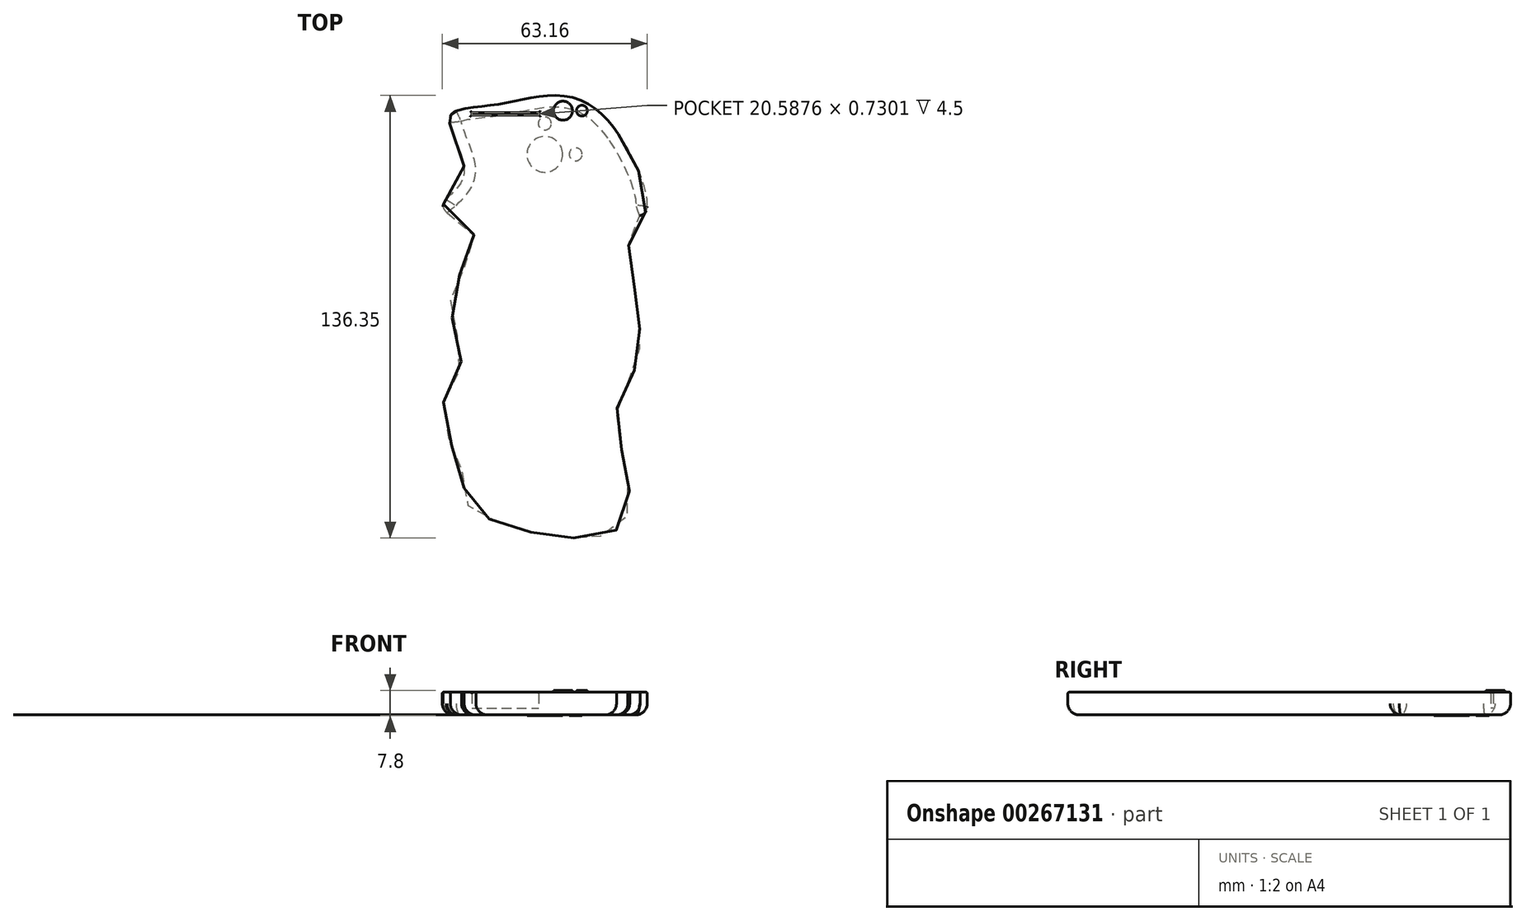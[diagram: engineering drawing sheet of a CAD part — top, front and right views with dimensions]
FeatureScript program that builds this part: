
annotation { "Feature Type Name" : "Feature", "Feature Type Description" : "" }
export const myFeature = defineFeature(function(context is Context, id is Id, definition is map)
    precondition{}
    {
        {
            var Q0;
            Q0=qCreatedBy(makeId("Top.planeOp"),FACE);
            var sketch = newSketch(context, id + "F0", { "sketchPlane" : qUnion([Q0])});
            skFitSpline(sketch, "E0", {"points": [v(-68.04, 102.87) * mm, v(-82.19, 98.83) * mm, v(-77.9, 80.9) * mm, v(-84.21, 71.3) * mm, v(-74.36, 61.95) * mm, v(-81.7, 44.48) * mm, v(-78.66, 23.47) * mm, v(-84.48, 9.04) * mm, v(-77.9, -12.47) * mm, v(-75.88, -21.33) * mm, v(-29.8, -27.4) * mm, v(-30.82, 7.58) * mm, v(-23.77, 26.7) * mm, v(-26.54, 66.97) * mm, v(-21.76, 69.99) * mm, v(-38.11, 102.2) * mm, v(-68.04, 102.87) * mm]});
            skArc(sketch, "E1", {"start": v(-30.24, 93.84) * mm, "mid": v(-56.07, 97.58) * mm, "end": v(-82.17, 97.08) * mm});
            skCircle(sketch, "E2", {"center": v(-47.33, 101) * mm, "radius": 2.92 * mm});
            skCircle(sketch, "E3", {"center": v(-41.48, 101) * mm, "radius": 1.66 * mm});
            skLineSegment(sketch, "E4.bottom", {"start": v(-75.36, 100.41) * mm, "end": v(-54.77, 100.41) * mm});
            skLineSegment(sketch, "E4.top", {"start": v(-75.36, 99.68) * mm, "end": v(-54.77, 99.68) * mm});
            skLineSegment(sketch, "E4.left", {"start": v(-75.36, 100.41) * mm, "end": v(-75.36, 99.68) * mm});
            skLineSegment(sketch, "E4.right", {"start": v(-54.77, 100.41) * mm, "end": v(-54.77, 99.68) * mm});
            skSolve(sketch);
        }
        {
            var Q0;
            {var subQ0=sQuery(id+"F0.wireOp",EDGE,"E1");Q0=makeQuery(id+"F0.imprint","IMPRINT",FACE,{"disambiguationData":[TD([[makeQuery(id+"F0.imprint","IMPRINT",EDGE,{"derivedFrom":subQ0}),1.0]])]});}
            var Q1;
            {var subQ0=sQuery(id+"F0.wireOp",EDGE,"E1");Q1=makeQuery(id+"F0.imprint","IMPRINT",FACE,{"disambiguationData":[TD([[makeQuery(id+"F0.imprint","IMPRINT",EDGE,{"derivedFrom":subQ0}),-1.0]])]});}
            extrude(context, id + "F1", {"entities" : qUnion([Q0, Q1]), "depth" : 5 * mm});
        }
        {
            var Q0;
            Q0=makeQuery(id+"F0.imprint","IMPRINT",FACE,{"disambiguationData":[TD([[makeQuery(id+"F0.imprint","IMPRINT",EDGE,{"derivedFrom":sQuery(id+"F0.wireOp",EDGE,"E4.bottom")}),-1.0]])]});
            var Q1;
            Q1=makeQuery(id+"F1.opExtrude","CAP_FACE",FACE,{"disambiguationData":[OSD([sQuery(id+"F0.wireOp",EDGE,"E0"),sQuery(id+"F0.wireOp",EDGE,"E4.bottom"),sQuery(id+"F0.wireOp",EDGE,"E4.top"),sQuery(id+"F0.wireOp",EDGE,"E4.left"),sQuery(id+"F0.wireOp",EDGE,"E4.right")])],"isStart":false});
            extrude(context, id + "F2", {"entities" : qUnion([Q0, Q1]), "operationType" : NewBodyOperationType.ADD, "depth" : 2 * mm});
        }
        {
            var Q0;
            Q0=makeQuery(id+"F0.imprint","IMPRINT",FACE,{"disambiguationData":[TD([[makeQuery(id+"F0.imprint","IMPRINT",EDGE,{"derivedFrom":sQuery(id+"F0.wireOp",EDGE,"E2")}),1.0]])]});
            var Q1;
            Q1=makeQuery(id+"F0.imprint","IMPRINT",FACE,{"disambiguationData":[TD([[makeQuery(id+"F0.imprint","IMPRINT",EDGE,{"derivedFrom":sQuery(id+"F0.wireOp",EDGE,"E3")}),1.0]])]});
            extrude(context, id + "F3", {"entities" : qUnion([Q0, Q1]), "operationType" : NewBodyOperationType.ADD, "depth" : 7.5 * mm});
        }
        {
            var Q0;
            Q0=makeQuery(id+"F2.opExtrude","CAP_FACE",FACE,{"disambiguationData":[OSD([sQuery(id+"F0.wireOp",EDGE,"E0"),sQuery(id+"F0.wireOp",EDGE,"E2"),sQuery(id+"F0.wireOp",EDGE,"E3"),sQuery(id+"F0.wireOp",EDGE,"E4.bottom"),sQuery(id+"F0.wireOp",EDGE,"E4.top"),sQuery(id+"F0.wireOp",EDGE,"E4.left"),sQuery(id+"F0.wireOp",EDGE,"E4.right")])],"isStart":false});
            fillet(context, id + "F4", {"entities" : qUnion([Q0]), "radius" : 0.5 * mm, "tangentPropagation" : true, "allowEdgeOverflow" : false});
        }
        {
            var Q0;
            {var subQ0=sQuery(id+"F0.wireOp",EDGE,"E1");Q0=makeQuery(id+"F0.imprint","IMPRINT",FACE,{"disambiguationData":[TD([[makeQuery(id+"F0.imprint","IMPRINT",EDGE,{"derivedFrom":subQ0}),1.0]])]});}
            extrude(context, id + "F5", {"entities" : qUnion([Q0]), "operationType" : NewBodyOperationType.ADD, "depth" : 0.1 * mm});
        }
        {
            var Q0;
            {var subQ0=sQuery(id+"F0.wireOp",EDGE,"E3");var subQ1=sQuery(id+"F0.wireOp",EDGE,"E2");var subQ2=sQuery(id+"F0.wireOp",EDGE,"E4.right");var subQ3=sQuery(id+"F0.wireOp",EDGE,"E4.left");var subQ4=sQuery(id+"F0.wireOp",EDGE,"E4.top");var subQ5=sQuery(id+"F0.wireOp",EDGE,"E4.bottom");Q0=makeQuery(id+"F3.boolean.opBoolean","MERGE",FACE,{"derivedFrom":[makeQuery(id+"F2.boolean.opBoolean","MERGE",FACE,{"derivedFrom":[makeQuery(id+"F1.opExtrude","CAP_FACE",FACE,{"disambiguationData":[OSD([sQuery(id+"F0.wireOp",EDGE,"E0"),subQ1,subQ0,subQ5,subQ4,subQ3,subQ2])],"isStart":true}),makeQuery(id+"F2.opExtrude","CAP_FACE",FACE,{"disambiguationData":[OSD([subQ5,subQ4,subQ3,subQ2])],"isStart":true})]}),makeQuery(id+"F3.opExtrude","CAP_FACE",FACE,{"disambiguationData":[OSD([subQ1])],"isStart":true}),makeQuery(id+"F3.opExtrude","CAP_FACE",FACE,{"disambiguationData":[OSD([subQ0])],"isStart":true})]});}
            fillet(context, id + "F6", {"entities" : qUnion([Q0]), "radius" : 3.5 * mm, "tangentPropagation" : true, "allowEdgeOverflow" : false});
        }
        {
            var Q0;
            Q0=qCreatedBy(makeId("Right.planeOp"),FACE);
            cPlane(context, id + "F7", {"entities" : qUnion([Q0]), "cplaneType" : CPlaneType.OFFSET, "offset" : 30 * mm, "oppositeDirection" : true, "width" : 150 * mm, "height" : 150 * mm});
        }
        {
            var Q0;
            Q0=qCreatedBy(id+"F7.planeOp",FACE);
            var sketch = newSketch(context, id + "F8", { "sketchPlane" : qUnion([Q0])});
            skPoint(sketch, "E5.orphan", {"position": v(44.2, 4.87) * mm});
            skPoint(sketch, "E6.start.orphan", {"position": v(44.2, 3.37) * mm});
            skCircle(sketch, "E7", {"center": v(45.65, 4.88) * mm, "radius": 1 * mm});
            skCircle(sketch, "E8", {"center": v(50.65, 4.88) * mm, "radius": 1 * mm});
            skPoint(sketch, "E9.orphan", {"position": v(49.65, 4.88) * mm});
            skLineSegment(sketch, "E10", {"start": v(44.65, 4.97) * mm, "end": v(46.64, 4.97) * mm});
            skLineSegment(sketch, "E11", {"start": v(46.64, 4.97) * mm, "end": v(46.64, 4.78) * mm});
            skLineSegment(sketch, "E12", {"start": v(46.64, 4.78) * mm, "end": v(44.65, 4.78) * mm});
            skLineSegment(sketch, "E13", {"start": v(50.52, 5.87) * mm, "end": v(50.52, 3.89) * mm});
            skLineSegment(sketch, "E14", {"start": v(50.52, 3.89) * mm, "end": v(50.77, 3.89) * mm});
            skLineSegment(sketch, "E15", {"start": v(50.77, 3.89) * mm, "end": v(50.77, 5.87) * mm});
            skLineSegment(sketch, "E16", {"start": v(49.65, 4.97) * mm, "end": v(51.64, 4.97) * mm});
            skLineSegment(sketch, "E17", {"start": v(51.64, 4.97) * mm, "end": v(51.64, 4.78) * mm});
            skLineSegment(sketch, "E18", {"start": v(51.64, 4.78) * mm, "end": v(49.65, 4.78) * mm});
            skSolve(sketch);
        }
        {
            var Q0;
            Q0=sQuery(id+"F8.wireOp",EDGE,"E7");
            extrude(context, id + "F9", {"bodyType" : ToolBodyType.SURFACE, "surfaceEntities" : qUnion([Q0]), "depth" : 5.2 * mm});
        }
        {
            var Q0;
            Q0=sQuery(id+"F8.wireOp",EDGE,"E8");
            extrude(context, id + "F10", {"bodyType" : ToolBodyType.SURFACE, "surfaceEntities" : qUnion([Q0]), "depth" : 4.5 * mm});
        }
        {
            var Q0;
            Q0=qCreatedBy(makeId("Right.planeOp"),FACE);
            cPlane(context, id + "F11", {"entities" : qUnion([Q0]), "cplaneType" : CPlaneType.OFFSET, "offset" : 68.7 * mm, "oppositeDirection" : true, "width" : 150 * mm, "height" : 150 * mm});
        }
        {
            var Q0;
            Q0=qCreatedBy(id+"F11.planeOp",FACE);
            var sketch = newSketch(context, id + "F12", { "sketchPlane" : qUnion([Q0])});
            skLineSegment(sketch, "E19", {"start": v(72.37, 3.86) * mm, "end": v(70.8, 3.86) * mm});
            skPoint(sketch, "E20.start.orphan", {"position": v(70.8, 5.7) * mm});
            skPoint(sketch, "E21.start.orphan", {"position": v(72.37, 5.7) * mm});
            skLineSegment(sketch, "E22", {"start": v(72.37, 3.86) * mm, "end": v(72.37, 6.13) * mm});
            skLineSegment(sketch, "E23", {"start": v(72.37, 6.13) * mm, "end": v(70.8, 6.13) * mm});
            skLineSegment(sketch, "E24", {"start": v(70.8, 6.13) * mm, "end": v(70.8, 3.86) * mm});
            skSolve(sketch);
        }
        {
            var Q0;
            Q0=sQuery(id+"F12.wireOp",EDGE,"E24");
            var Q1;
            Q1=sQuery(id+"F12.wireOp",EDGE,"E23");
            var Q2;
            Q2=sQuery(id+"F12.wireOp",EDGE,"E19");
            var Q3;
            Q3=sQuery(id+"F12.wireOp",EDGE,"E22");
            extrude(context, id + "F13", {"bodyType" : ToolBodyType.SURFACE, "surfaceEntities" : qUnion([Q0, Q1, Q2, Q3]), "oppositeDirection" : true, "depth" : 16 * mm});
        }
        {
            var Q0;
            Q0=qCreatedBy(makeId("Top.planeOp"),FACE);
            var sketch = newSketch(context, id + "F14", { "sketchPlane" : qUnion([Q0])});
            skCircle(sketch, "E25", {"center": v(-52.9, 87.55) * mm, "radius": 5.5 * mm});
            skCircle(sketch, "E26", {"center": v(-52.9, 97.05) * mm, "radius": 2 * mm});
            skCircle(sketch, "E27", {"center": v(-43.4, 87.55) * mm, "radius": 2 * mm});
            skSolve(sketch);
        }
        {
            var Q0;
            Q0=makeQuery(id+"F14.imprint","IMPRINT",FACE,{"disambiguationData":[TD([[makeQuery(id+"F14.imprint","IMPRINT",EDGE,{"derivedFrom":sQuery(id+"F14.wireOp",EDGE,"E25")}),1.0]])]});
            var Q1;
            Q1=makeQuery(id+"F14.imprint","IMPRINT",FACE,{"disambiguationData":[TD([[makeQuery(id+"F14.imprint","IMPRINT",EDGE,{"derivedFrom":sQuery(id+"F14.wireOp",EDGE,"E26")}),1.0]])]});
            var Q2;
            Q2=makeQuery(id+"F14.imprint","IMPRINT",FACE,{"disambiguationData":[TD([[makeQuery(id+"F14.imprint","IMPRINT",EDGE,{"derivedFrom":sQuery(id+"F14.wireOp",EDGE,"E27")}),1.0]])]});
            extrude(context, id + "F15", {"entities" : qUnion([Q0, Q1, Q2]), "operationType" : NewBodyOperationType.ADD, "oppositeDirection" : true, "depth" : 0.3 * mm});
        }
    });
